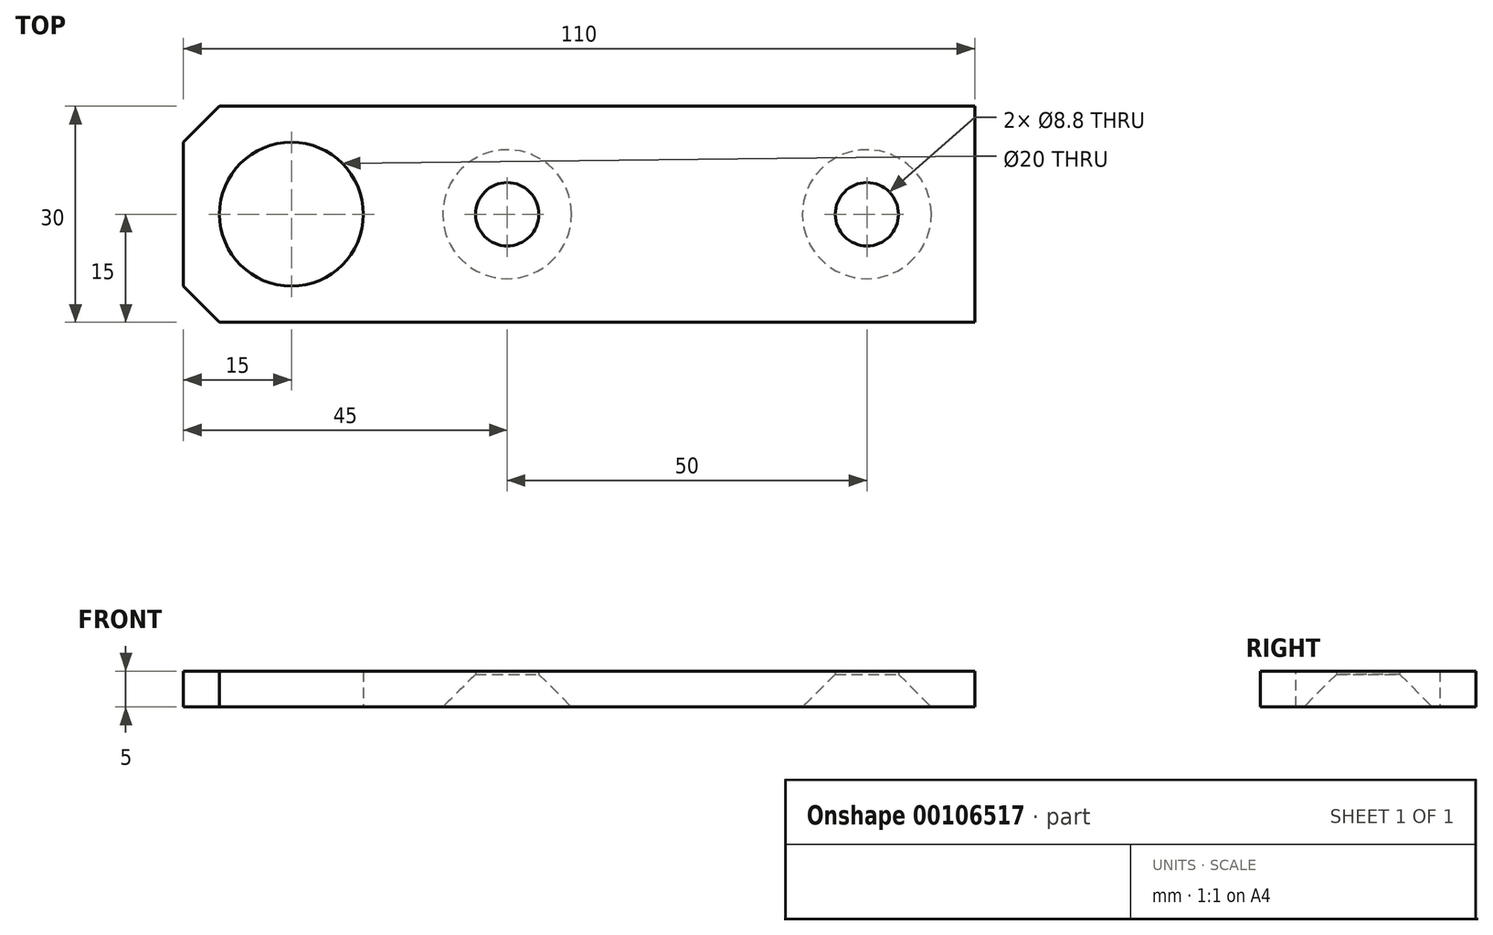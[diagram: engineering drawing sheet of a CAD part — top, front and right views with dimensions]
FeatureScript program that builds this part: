
annotation { "Feature Type Name" : "Feature", "Feature Type Description" : "" }
export const myFeature = defineFeature(function(context is Context, id is Id, definition is map)
    precondition{}
    {
        {
            var Q0;
            Q0=qCreatedBy(makeId("Top.planeOp"),FACE);
            var sketch = newSketch(context, id + "F0", { "sketchPlane" : qUnion([Q0])});
            skLineSegment(sketch, "E0.bottom", {"start": v(0, 0) * mm, "end": v(110, 0) * mm});
            skLineSegment(sketch, "E0.top", {"start": v(0, 30) * mm, "end": v(110, 30) * mm});
            skLineSegment(sketch, "E0.left", {"start": v(0, 0) * mm, "end": v(0, 30) * mm});
            skLineSegment(sketch, "E0.right", {"start": v(110, 0) * mm, "end": v(110, 30) * mm});
            skCircle(sketch, "E1", {"center": v(15, 15) * mm, "radius": 10 * mm});
            skPoint(sketch, "E2", {"position": v(45, 15) * mm});
            skPoint(sketch, "E3", {"position": v(95, 15) * mm});
            skSolve(sketch);
        }
        {
            var Q0;
            Q0=makeQuery(id+"F0.imprint","IMPRINT",FACE,{"disambiguationData":[TD([[makeQuery(id+"F0.imprint","IMPRINT",EDGE,{"derivedFrom":sQuery(id+"F0.wireOp",EDGE,"E0.bottom")}),1.0]])]});
            extrude(context, id + "F1", {"entities" : qUnion([Q0]), "depth" : 5 * mm});
        }
        {
            var Q0;
            Q0=makeQuery(id+"F1.opExtrude","SWEPT_EDGE",EDGE,{"disambiguationData":[OSD([sQuery(id+"F0.wireOp",EDGE,"E0.top"),sQuery(id+"F0.wireOp",EDGE,"E0.left")])]});
            var Q1;
            Q1=makeQuery(id+"F1.opExtrude","SWEPT_EDGE",EDGE,{"disambiguationData":[OSD([sQuery(id+"F0.wireOp",EDGE,"E0.bottom"),sQuery(id+"F0.wireOp",EDGE,"E0.left")])]});
            chamfer(context, id + "F2", {"entities" : qUnion([Q0, Q1]), "width" : 5 * mm, "tangentPropagation" : true});
        }
        {
            var Q0;
            Q0=sQuery(id+"F0.wireOp",VERTEX,"E3");
            var Q1;
            Q1=sQuery(id+"F0.wireOp",VERTEX,"E2");
            var Q2;
            Q2=makeQuery(id+"F1.opExtrude","SWEPT_BODY",BODY,{"disambiguationData":[OSD([sQuery(id+"F0.wireOp",EDGE,"E0.bottom"),sQuery(id+"F0.wireOp",EDGE,"E0.top"),sQuery(id+"F0.wireOp",EDGE,"E0.left"),sQuery(id+"F0.wireOp",EDGE,"E0.right"),sQuery(id+"F0.wireOp",EDGE,"E1")])]});
            hole(context, id + "F3", {"style" : HoleStyle.C_SINK, "endStyle" : HoleEndStyle.THROUGH, "oppositeDirection" : true, "standardTappedOrClearance" : lookupTablePath({ "standard" : "ISO", "fit" : "Normal", "size" : "M8", "type" : "Clearance" }), "standardBlindInLast" : lookupTablePath({ "fit" : "Standard", "standard" : "ISO", "size" : "M8", "type" : "Clearance" }), "holeDiameter" : 8.8 * mm, "cSinkDiameter" : 17.92 * mm, "cSinkAngle" : 90 * degree, "locations" : qUnion([Q0, Q1]), "scope" : qUnion([Q2]), "isTappedThrough" : true});
        }
    });
